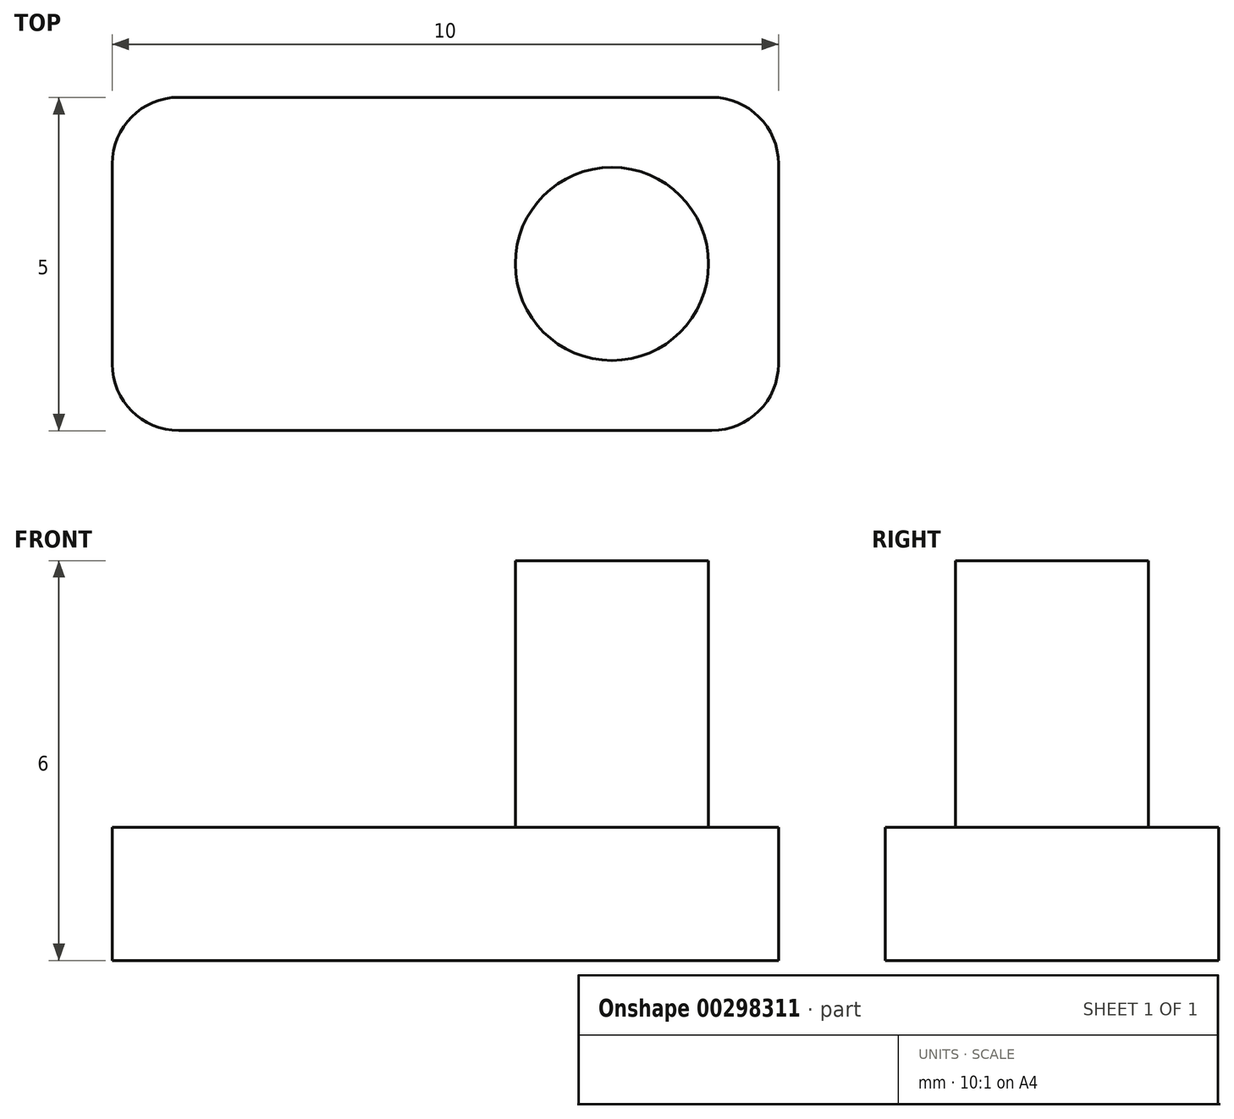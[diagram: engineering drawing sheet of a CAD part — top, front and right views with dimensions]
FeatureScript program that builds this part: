
annotation { "Feature Type Name" : "Feature", "Feature Type Description" : "" }
export const myFeature = defineFeature(function(context is Context, id is Id, definition is map)
    precondition{}
    {
        {
            var Q0;
            Q0=qCreatedBy(makeId("Top.planeOp"),FACE);
            var sketch = newSketch(context, id + "F0", { "sketchPlane" : qUnion([Q0])});
            skLineSegment(sketch, "E0.bottom", {"start": v(-59.44, -11.95) * mm, "end": v(-67.44, -11.95) * mm});
            skLineSegment(sketch, "E0.top", {"start": v(-59.44, -6.95) * mm, "end": v(-67.44, -6.95) * mm});
            skLineSegment(sketch, "E0.left", {"start": v(-58.44, -10.95) * mm, "end": v(-58.44, -7.95) * mm});
            skLineSegment(sketch, "E0.right", {"start": v(-68.44, -10.95) * mm, "end": v(-68.44, -7.95) * mm});
            skPoint(sketch, "E0.middle", {"position": v(-63.44, -9.45) * mm});
            skPoint(sketch, "E1.visualSharp", {"position": v(-58.44, -6.95) * mm});
            skArc(sketch, "E1.filletArc", {"start": v(-58.44, -7.95) * mm, "mid": v(-58.73, -7.24) * mm, "end": v(-59.44, -6.95) * mm});
            skPoint(sketch, "E2.visualSharp", {"position": v(-68.44, -6.95) * mm});
            skArc(sketch, "E2.filletArc", {"start": v(-67.44, -6.95) * mm, "mid": v(-68.15, -7.24) * mm, "end": v(-68.44, -7.95) * mm});
            skPoint(sketch, "E3.visualSharp", {"position": v(-68.44, -11.95) * mm});
            skArc(sketch, "E3.filletArc", {"start": v(-68.44, -10.95) * mm, "mid": v(-68.15, -11.65) * mm, "end": v(-67.44, -11.95) * mm});
            skPoint(sketch, "E4.visualSharp", {"position": v(-58.44, -11.95) * mm});
            skArc(sketch, "E4.filletArc", {"start": v(-59.44, -11.95) * mm, "mid": v(-58.73, -11.65) * mm, "end": v(-58.44, -10.95) * mm});
            skSolve(sketch);
        }
        {
            var Q0;
            Q0 = qSketchRegion(id + "F0", true);
            extrude(context, id + "F1", {"entities" : qUnion([Q0]), "depth" : 2 * mm});
        }
        {
            var Q0;
            Q0=makeQuery(id+"F1.opExtrude","CAP_FACE",FACE,{"disambiguationData":[OSD([sQuery(id+"F0.wireOp",EDGE,"E0.bottom"),sQuery(id+"F0.wireOp",EDGE,"E0.top"),sQuery(id+"F0.wireOp",EDGE,"E0.left"),sQuery(id+"F0.wireOp",EDGE,"E0.right")])],"isStart":false});
            var sketch = newSketch(context, id + "F2", { "sketchPlane" : qUnion([Q0])});
            skCircle(sketch, "E5", {"center": v(-60.94, -9.45) * mm, "radius": 1.45 * mm});
            skSolve(sketch);
        }
        {
            var Q0;
            Q0 = qSketchRegion(id + "F2", true);
            extrude(context, id + "F3", {"entities" : qUnion([Q0]), "operationType" : NewBodyOperationType.ADD, "depth" : 4 * mm});
        }
    });
